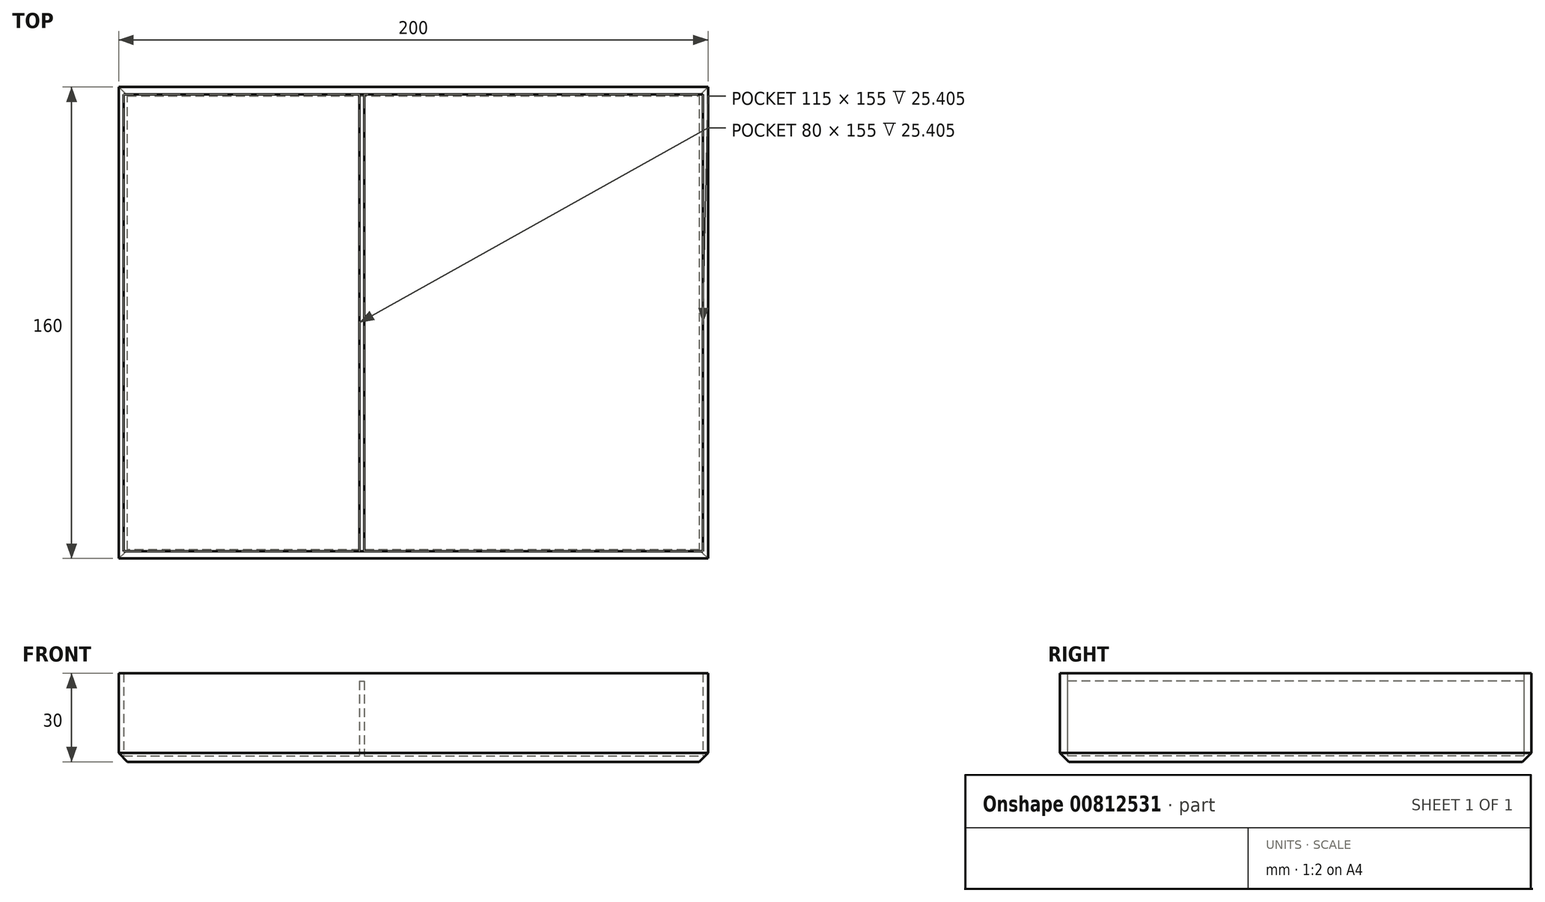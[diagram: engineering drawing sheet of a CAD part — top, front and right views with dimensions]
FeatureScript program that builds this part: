
annotation { "Feature Type Name" : "Feature", "Feature Type Description" : "" }
export const myFeature = defineFeature(function(context is Context, id is Id, definition is map)
    precondition{}
    {
        {
            var Q0;
            Q0=qCreatedBy(makeId("Front.planeOp"),FACE);
            var sketch = newSketch(context, id + "F0", { "sketchPlane" : qUnion([Q0])});
            skLineSegment(sketch, "E0.bottom", {"start": v(0, 0) * mm, "end": v(200, 0) * mm});
            skLineSegment(sketch, "E0.top", {"start": v(0, 30) * mm, "end": v(200, 30) * mm});
            skLineSegment(sketch, "E0.left", {"start": v(0, 0) * mm, "end": v(0, 30) * mm});
            skLineSegment(sketch, "E0.right", {"start": v(200, 0) * mm, "end": v(200, 30) * mm});
            skSolve(sketch);
        }
        {
            var Q0;
            Q0=makeQuery(id+"F0.imprint","IMPRINT",FACE,{"disambiguationData":[TD([[makeQuery(id+"F0.imprint","IMPRINT",EDGE,{"derivedFrom":sQuery(id+"F0.wireOp",EDGE,"E0.bottom")}),1.0]])]});
            extrude(context, id + "F1", {"entities" : qUnion([Q0]), "endBound" : BoundingType.SYMMETRIC, "depth" : 160 * mm, "offsetDistance" : 25 * mm});
        }
        {
            var Q0;
            Q0=qCreatedBy(makeId("Front.planeOp"),FACE);
            var sketch = newSketch(context, id + "F2", { "sketchPlane" : qUnion([Q0])});
            skLineSegment(sketch, "E1.bottom", {"start": v(1.66, 30.96) * mm, "end": v(81.66, 30.96) * mm});
            skLineSegment(sketch, "E1.top", {"start": v(1.66, 1.96) * mm, "end": v(81.66, 1.96) * mm});
            skLineSegment(sketch, "E1.left", {"start": v(1.66, 30.96) * mm, "end": v(1.66, 1.96) * mm});
            skLineSegment(sketch, "E1.right", {"start": v(81.66, 30.96) * mm, "end": v(81.66, 1.96) * mm});
            skLineSegment(sketch, "E2.bottom", {"start": v(81, 30.96) * mm, "end": v(85.63, 30.96) * mm});
            skLineSegment(sketch, "E2.top", {"start": v(81, 27.37) * mm, "end": v(85.63, 27.37) * mm});
            skLineSegment(sketch, "E2.left", {"start": v(85.63, 30.96) * mm, "end": v(85.63, 27.37) * mm});
            skLineSegment(sketch, "E2.right", {"start": v(81, 30.96) * mm, "end": v(81, 27.37) * mm});
            skLineSegment(sketch, "E3.bottom", {"start": v(83.32, 30.96) * mm, "end": v(198.32, 30.96) * mm});
            skLineSegment(sketch, "E3.top", {"start": v(83.32, 1.96) * mm, "end": v(198.32, 1.96) * mm});
            skLineSegment(sketch, "E3.left", {"start": v(83.32, 30.96) * mm, "end": v(83.32, 1.96) * mm});
            skLineSegment(sketch, "E3.right", {"start": v(198.32, 30.96) * mm, "end": v(198.32, 1.96) * mm});
            skSolve(sketch);
        }
        {
            var Q0;
            Q0 = qSketchRegion(id + "F2", true);
            extrude(context, id + "F3", {"entities" : qUnion([Q0]), "operationType" : NewBodyOperationType.REMOVE, "endBound" : BoundingType.SYMMETRIC, "oppositeDirection" : true, "depth" : 155 * mm, "offsetDistance" : 25 * mm});
        }
        {
            var Q0;
            Q0=makeQuery(id+"F1.opExtrude","CAP_EDGE",EDGE,{"disambiguationData":[OSD([sQuery(id+"F0.wireOp",EDGE,"E0.bottom")])],"isStart":false});
            var Q1;
            Q1=makeQuery(id+"F1.opExtrude","SWEPT_EDGE",EDGE,{"disambiguationData":[OSD([sQuery(id+"F0.wireOp",EDGE,"E0.bottom"),sQuery(id+"F0.wireOp",EDGE,"E0.left")])]});
            var Q2;
            Q2=makeQuery(id+"F1.opExtrude","CAP_EDGE",EDGE,{"disambiguationData":[OSD([sQuery(id+"F0.wireOp",EDGE,"E0.bottom")])],"isStart":true});
            var Q3;
            Q3=makeQuery(id+"F1.opExtrude","SWEPT_EDGE",EDGE,{"disambiguationData":[OSD([sQuery(id+"F0.wireOp",EDGE,"E0.bottom"),sQuery(id+"F0.wireOp",EDGE,"E0.right")])]});
            chamfer(context, id + "F4", {"entities" : qUnion([Q0, Q1, Q2, Q3]), "width" : 3 * mm, "tangentPropagation" : true});
        }
    });
